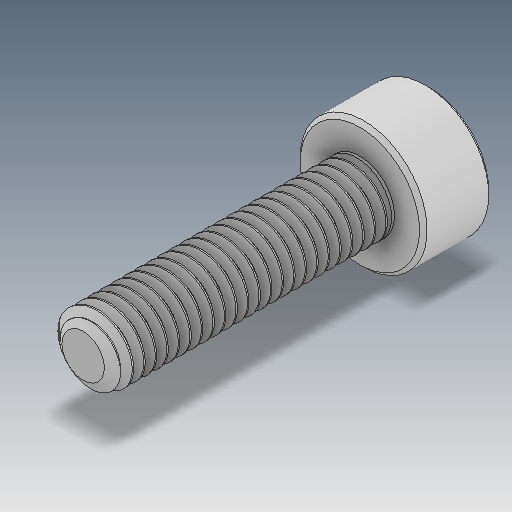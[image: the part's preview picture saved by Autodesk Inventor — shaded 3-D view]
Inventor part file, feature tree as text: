
AUTODESK INVENTOR PART (.ipt)
format: ipt  version: 2020 (Build 240168000, 168)  size: 869,888 bytes
history: native  units: in
note: dims shown in document units (in); Inventor stores cm internally (conversion verified against a paired STEP export)
features: revolve x1
ambient origin geometry x8: Origin, YZ Plane, XZ Plane, XY Plane, X Axis, Y Axis, Z Axis, Center Point
bodies: Solid1 (feature_tree)
feature tree (1):
  revolve  "Revolve1"  [1 undecoded]
note: 1 required parameter value undecoded (feature->parameter linkage not recoverable at this tier; creation-order binding heuristic only, values carry confidence <= 0.55)
